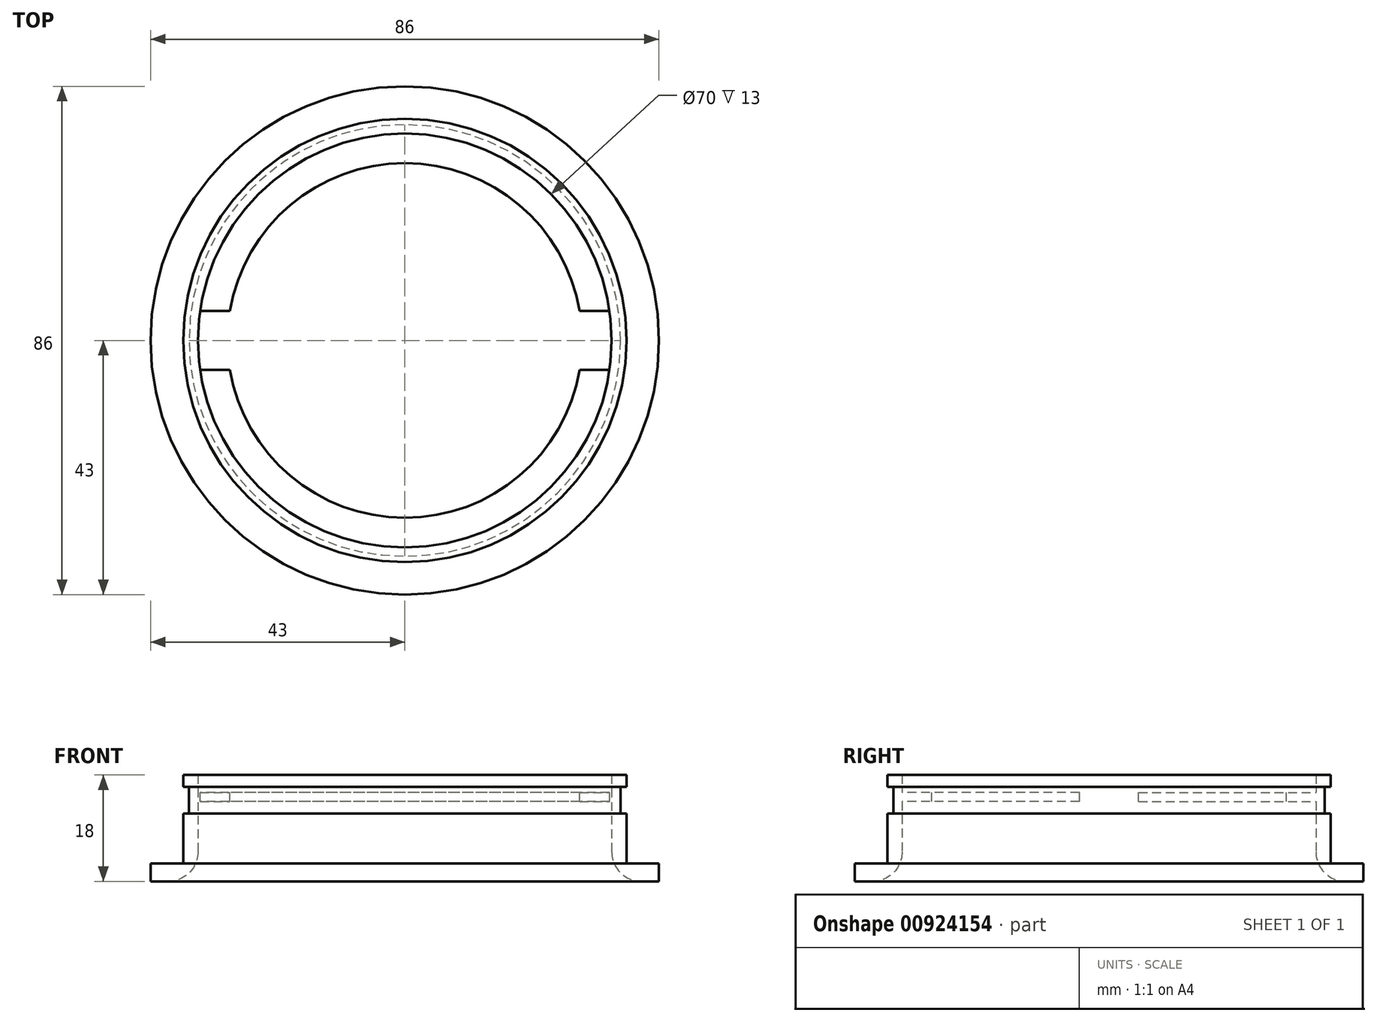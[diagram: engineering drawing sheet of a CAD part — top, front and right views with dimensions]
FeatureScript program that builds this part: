
annotation { "Feature Type Name" : "Feature", "Feature Type Description" : "" }
export const myFeature = defineFeature(function(context is Context, id is Id, definition is map)
    precondition{}
    {
        {
            var Q0;
            Q0=qCreatedBy(makeId("Top.planeOp"),FACE);
            var sketch = newSketch(context, id + "F0", { "sketchPlane" : qUnion([Q0])});
            skCircle(sketch, "E0", {"center": v(0, 0) * mm, "radius": 35 * mm});
            skCircle(sketch, "E1", {"center": v(0, 0) * mm, "radius": 37.5 * mm});
            skSolve(sketch);
        }
        {
            var Q0;
            Q0 = qSketchRegion(id + "F0", true);
            extrude(context, id + "F1", {"entities" : qUnion([Q0]), "depth" : 18 * mm, "offsetDistance" : 25 * mm});
        }
        {
            var Q0;
            Q0=qCreatedBy(makeId("Top.planeOp"),FACE);
            var sketch = newSketch(context, id + "F2", { "sketchPlane" : qUnion([Q0])});
            skCircle(sketch, "E2", {"center": v(0, 0) * mm, "radius": 43 * mm});
            skCircle(sketch, "E3", {"center": v(0, 0) * mm, "radius": 35 * mm});
            skSolve(sketch);
        }
        {
            var Q0;
            Q0 = qSketchRegion(id + "F2", true);
            extrude(context, id + "F3", {"entities" : qUnion([Q0]), "operationType" : NewBodyOperationType.ADD, "depth" : 3 * mm, "offsetDistance" : 25 * mm});
        }
        {
            var Q0;
            Q0=makeQuery(id+"F1.opExtrude","CAP_EDGE",EDGE,{"disambiguationData":[OSD([sQuery(id+"F0.wireOp",EDGE,"E0")])],"isStart":true});
            fillet(context, id + "F4", {"entities" : qUnion([Q0]), "radius" : 5 * mm, "tangentPropagation" : true, "allowEdgeOverflow" : false});
        }
        {
            var Q0;
            Q0=makeQuery(id+"F1.opExtrude","CAP_FACE",FACE,{"disambiguationData":[OSD([sQuery(id+"F0.wireOp",EDGE,"E0"),sQuery(id+"F0.wireOp",EDGE,"E1")])],"isStart":false});
            cPlane(context, id + "F5", {"entities" : qUnion([Q0]), "cplaneType" : CPlaneType.OFFSET, "offset" : 2 * mm, "oppositeDirection" : true, "width" : 150 * mm, "height" : 150 * mm});
        }
        {
            var Q0;
            Q0=qCreatedBy(id+"F5.planeOp",FACE);
            var sketch = newSketch(context, id + "F6", { "sketchPlane" : qUnion([Q0])});
            skCircle(sketch, "E4", {"center": v(0, 0) * mm, "radius": 37.5 * mm});
            skCircle(sketch, "E5", {"center": v(0, 0) * mm, "radius": 36.5 * mm});
            skSolve(sketch);
        }
        {
            var Q0;
            Q0 = qSketchRegion(id + "F6", true);
            extrude(context, id + "F7", {"entities" : qUnion([Q0]), "operationType" : NewBodyOperationType.REMOVE, "oppositeDirection" : true, "depth" : 4.5 * mm, "offsetDistance" : 25 * mm});
        }
        {
            var Q0;
            Q0=makeQuery(id+"F1.opExtrude","CAP_FACE",FACE,{"disambiguationData":[OSD([sQuery(id+"F0.wireOp",EDGE,"E0"),sQuery(id+"F0.wireOp",EDGE,"E1")])],"isStart":false});
            cPlane(context, id + "F8", {"entities" : qUnion([Q0]), "cplaneType" : CPlaneType.OFFSET, "offset" : 3 * mm, "oppositeDirection" : true, "width" : 150 * mm, "height" : 150 * mm});
        }
        {
            var Q0;
            Q0=qCreatedBy(id+"F8.planeOp",FACE);
            var sketch = newSketch(context, id + "F9", { "sketchPlane" : qUnion([Q0])});
            skArc(sketch, "E6", {"start": v(34.64, 5) * mm, "mid": v(0, 35) * mm, "end": v(-34.64, 5) * mm});
            skArc(sketch, "E7.0", {"start": v(29.58, 5) * mm, "mid": v(0, 30) * mm, "end": v(-29.58, 5) * mm});
            skLineSegment(sketch, "E8", {"start": v(-34.64, 5) * mm, "end": v(-29.58, 5) * mm});
            skLineSegment(sketch, "E9", {"start": v(29.58, 5) * mm, "end": v(34.64, 5) * mm});
            skArc(sketch, "E10.MirrorCS", {"start": v(29.58, -5) * mm, "mid": v(0, -30) * mm, "end": v(-29.58, -5) * mm});
            skLineSegment(sketch, "E11.MirrorCS", {"start": v(-34.64, -5) * mm, "end": v(-29.58, -5) * mm});
            skLineSegment(sketch, "E12.MirrorCS", {"start": v(29.58, -5) * mm, "end": v(34.64, -5) * mm});
            skArc(sketch, "E13.MirrorCS", {"start": v(34.64, -5) * mm, "mid": v(0, -35) * mm, "end": v(-34.64, -5) * mm});
            skSolve(sketch);
        }
        {
            var Q0;
            Q0 = qSketchRegion(id + "F9", true);
            extrude(context, id + "F10", {"entities" : qUnion([Q0]), "operationType" : NewBodyOperationType.ADD, "oppositeDirection" : true, "depth" : 1.5 * mm, "offsetDistance" : 25 * mm});
        }
    });
